# Revit family: Kitchen_Taps-Mixers_hansgrohe_72804000-Talis-M54-Single-lever-kitchen_
name_source: partatom
category: Plumbing Fixtures
revit_build: Autodesk Revit 2015 (Build: 20140903_1530(x64)
units: mm (PartAtom-declared; Revit-internal decimal feet)

## types (1)
- Chrome 000
    BIMobject category = Taps & Mixers
    BIMobject category code = kitchen-taps
    BIMobject main category = Kitchen
    BIMobject main category code = kitchen
    Brand url = http://www.hansgrohe-int.com
    Default Elevation = 1219.2 mm  [stored 4 ft]
    Design country = Germany
    Edition number = 1
    GTIN code = https://4059625255339
    IFC Classification = Sanitary Terminal
    Installation instructions = https://www.hansgrohe.com
    Manufacturer country = Germany
    Manufacturer name = hansgrohe
    Material main = Chrome
    NBS Reference Code = 31-75
    NBS Reference Description = Sanitary Accessories
    Product Guid = 1b3e250c-11f2-47f0-bca8-0c8865307482
    Product SKU = 72804000
    Product data url = https://bimobject.com
    Product family = Talis M54
    Product group = Kitchen mixers
    Product name = 72804000 Talis M54 Single lever kitchen mixer 220, 1jet
    Product url = https://www.hansgrohe.com
    QR code = http://bimobject.com
    Technical description = https://www.hansgrohe.com
    UNSPSC Code = 301815
    Uniclass 2.0 Code = PR-31-75
    Uniclass 2.0 Description = Sanitary Accessories

note: [stored X ft] marks values corroborated as IEEE doubles in the binary element streams (Revit-internal decimal feet)

## geometry (parser evidence)
native form markers: Sweep x3
no freeform markers — native parametric forms only
